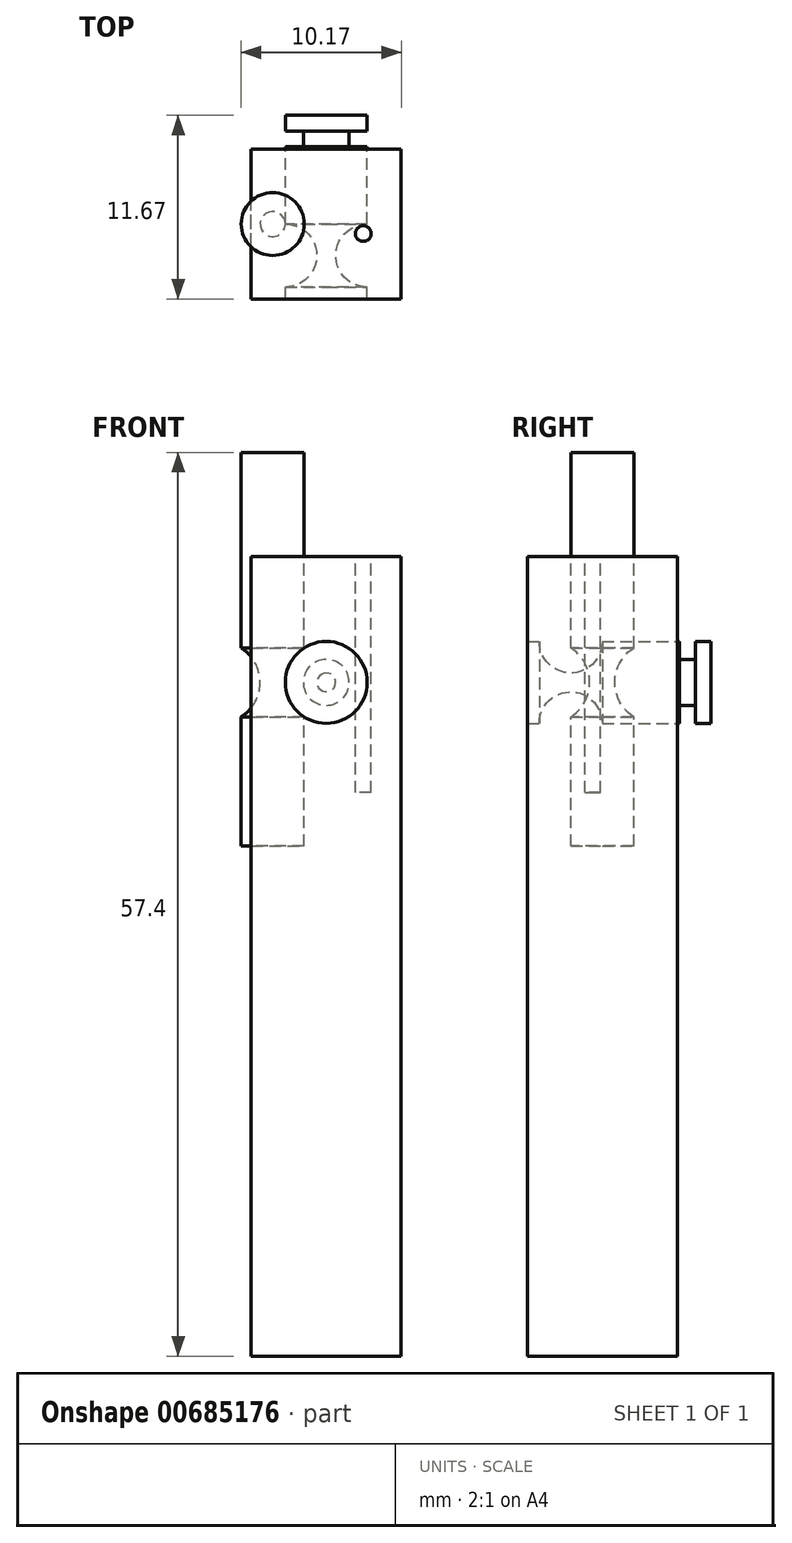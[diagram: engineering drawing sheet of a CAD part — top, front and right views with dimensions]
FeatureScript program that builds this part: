
annotation { "Feature Type Name" : "Feature", "Feature Type Description" : "" }
export const myFeature = defineFeature(function(context is Context, id is Id, definition is map)
    precondition{}
    {
        {
            var Q0;
            Q0=qCreatedBy(makeId("Top.planeOp"),FACE);
            var sketch = newSketch(context, id + "F0", { "sketchPlane" : qUnion([Q0])});
            skLineSegment(sketch, "E0.bottom", {"start": v(0, 0) * mm, "end": v(9.53, 0) * mm});
            skLineSegment(sketch, "E0.top", {"start": v(0, 9.53) * mm, "end": v(9.53, 9.53) * mm});
            skLineSegment(sketch, "E0.left", {"start": v(0, 0) * mm, "end": v(0, 9.53) * mm});
            skLineSegment(sketch, "E0.right", {"start": v(9.53, 0) * mm, "end": v(9.53, 9.53) * mm});
            skSolve(sketch);
        }
        {
            var Q0;
            Q0 = qSketchRegion(id + "F0", true);
            extrude(context, id + "F1", {"entities" : qUnion([Q0]), "depth" : 50.8 * mm, "offsetDistance" : 25 * mm});
        }
        {
            var Q0;
            Q0=makeQuery(id+"F1.opExtrude","CAP_FACE",FACE,{"disambiguationData":[OSD([sQuery(id+"F0.wireOp",EDGE,"E0.bottom"),sQuery(id+"F0.wireOp",EDGE,"E0.top"),sQuery(id+"F0.wireOp",EDGE,"E0.left"),sQuery(id+"F0.wireOp",EDGE,"E0.right")])],"isStart":false});
            cPlane(context, id + "F2", {"entities" : qUnion([Q0]), "cplaneType" : CPlaneType.OFFSET, "offset" : 8 * mm, "oppositeDirection" : true, "width" : 150 * mm, "height" : 150 * mm});
        }
        {
            var Q0;
            Q0=qCreatedBy(id+"F2.planeOp",FACE);
            var sketch = newSketch(context, id + "F3", { "sketchPlane" : qUnion([Q0])});
            skPoint(sketch, "E1.0", {"position": v(4.76, 9.53) * mm});
            skPoint(sketch, "E2.0", {"position": v(4.76, 0) * mm});
            skLineSegment(sketch, "E3", {"start": v(4.76, 18.5) * mm, "end": v(4.76, -10.38) * mm, "construction": true});
            skLineSegment(sketch, "E4", {"start": v(2.16, 11.67) * mm, "end": v(4.76, 11.67) * mm});
            skLineSegment(sketch, "E5", {"start": v(2.16, 11.67) * mm, "end": v(2.16, 10.67) * mm});
            skLineSegment(sketch, "E6", {"start": v(3.3, 10.67) * mm, "end": v(2.16, 10.67) * mm});
            skLineSegment(sketch, "E7", {"start": v(3.3, 10.67) * mm, "end": v(3.3, 9.67) * mm});
            skLineSegment(sketch, "E8", {"start": v(2.16, 9.67) * mm, "end": v(3.3, 9.67) * mm});
            skLineSegment(sketch, "E9", {"start": v(2.16, 9.67) * mm, "end": v(2.16, 4.76) * mm});
            skLineSegment(sketch, "E10", {"start": v(2.16, 0) * mm, "end": v(4.76, 0) * mm});
            skPoint(sketch, "E11.0", {"position": v(0, 4.76) * mm});
            skPoint(sketch, "E12.0", {"position": v(9.53, 4.76) * mm});
            skArc(sketch, "E13", {"start": v(2.16, 0.76) * mm, "mid": v(4.16, 2.76) * mm, "end": v(2.16, 4.76) * mm});
            skLineSegment(sketch, "E14.trimOffspring", {"start": v(2.16, 0.76) * mm, "end": v(2.16, 0) * mm});
            skLineSegment(sketch, "E15", {"start": v(4.76, 11.67) * mm, "end": v(4.76, 0) * mm});
            skSolve(sketch);
        }
        {
            var Q0;
            Q0 = qSketchRegion(id + "F3", true);
            var Q1;
            Q1=sQuery(id+"F3.wireOp",EDGE,"E3");
            revolve(context, id + "F4", {"surfaceOperationType" : NewSurfaceOperationType.NEW, "entities" : qUnion([Q0]), "axis" : qUnion([Q1]), "revolveType" : RevolveType.FULL});
        }
        {
            var Q0;
            Q0=makeQuery(id+"F1.opExtrude","CAP_EDGE",EDGE,{"disambiguationData":[OSD([sQuery(id+"F0.wireOp",EDGE,"E0.left")])],"isStart":false});
            cPoint(context, id + "F5", {"entities" : qUnion([Q0]), "parameter" : 0.5});
        }
        {
            var Q0;
            Q0=makeQuery(id+"F1.opExtrude","CAP_EDGE",EDGE,{"disambiguationData":[OSD([sQuery(id+"F0.wireOp",EDGE,"E0.right")])],"isStart":false});
            cPoint(context, id + "F6", {"entities" : qUnion([Q0]), "parameter" : 0.5});
        }
        {
            var Q0;
            Q0=makeQuery(id+"F1.opExtrude","CAP_EDGE",EDGE,{"disambiguationData":[OSD([sQuery(id+"F0.wireOp",EDGE,"E0.right")])],"isStart":true});
            cPoint(context, id + "F7", {"entities" : qUnion([Q0]), "parameter" : 0.5});
        }
        {
            var Q0;
            Q0 = qCreatedBy(id + "F5" ,VERTEX);
            var Q1;
            Q1 = qCreatedBy(id + "F6" ,VERTEX);
            var Q2;
            Q2 = qCreatedBy(id + "F7" ,VERTEX);
            cPlane(context, id + "F8", {"entities" : qUnion([Q0, Q1, Q2]), "cplaneType" : CPlaneType.THREE_POINT, "offset" : 25 * mm, "width" : 150 * mm, "height" : 150 * mm});
        }
        {
            var Q0;
            Q0=qCreatedBy(id+"F8.planeOp",FACE);
            var sketch = newSketch(context, id + "F9", { "sketchPlane" : qUnion([Q0])});
            skLineSegment(sketch, "E16", {"start": v(1.36, 59.7) * mm, "end": v(1.36, 31.28) * mm, "construction": true});
            skLineSegment(sketch, "E17.left", {"start": v(1.36, 57.4) * mm, "end": v(1.36, 32.4) * mm});
            skArc(sketch, "E18.0", {"start": v(3.36, 45) * mm, "mid": v(2.16, 42.8) * mm, "end": v(3.36, 40.6) * mm});
            skLineSegment(sketch, "E19.bottom", {"start": v(1.36, 57.4) * mm, "end": v(3.36, 57.4) * mm});
            skLineSegment(sketch, "E19.top", {"start": v(1.36, 32.4) * mm, "end": v(3.36, 32.4) * mm});
            skLineSegment(sketch, "E19.right", {"start": v(3.36, 57.4) * mm, "end": v(3.36, 45) * mm});
            skLineSegment(sketch, "E20.trimOffspring", {"start": v(3.36, 40.6) * mm, "end": v(3.36, 32.4) * mm});
            skSolve(sketch);
        }
        {
            var Q0;
            Q0 = qSketchRegion(id + "F9", true);
            var Q1;
            Q1=sQuery(id+"F9.wireOp",EDGE,"E16");
            revolve(context, id + "F10", {"surfaceOperationType" : NewSurfaceOperationType.NEW, "entities" : qUnion([Q0]), "axis" : qUnion([Q1]), "revolveType" : RevolveType.FULL});
        }
        {
            var Q0;
            Q0=makeQuery(id+"F1.opExtrude","CAP_FACE",FACE,{"disambiguationData":[OSD([sQuery(id+"F0.wireOp",EDGE,"E0.bottom"),sQuery(id+"F0.wireOp",EDGE,"E0.top"),sQuery(id+"F0.wireOp",EDGE,"E0.left"),sQuery(id+"F0.wireOp",EDGE,"E0.right")])],"isStart":false});
            var sketch = newSketch(context, id + "F11", { "sketchPlane" : qUnion([Q0])});
            skCircle(sketch, "E21", {"center": v(7.11, 4.16) * mm, "radius": 0.5 * mm});
            skSolve(sketch);
        }
        {
            var Q0;
            Q0 = qSketchRegion(id + "F11", true);
            extrude(context, id + "F12", {"entities" : qUnion([Q0]), "oppositeDirection" : true, "depth" : 15 * mm, "offsetDistance" : 25 * mm});
        }
    });
